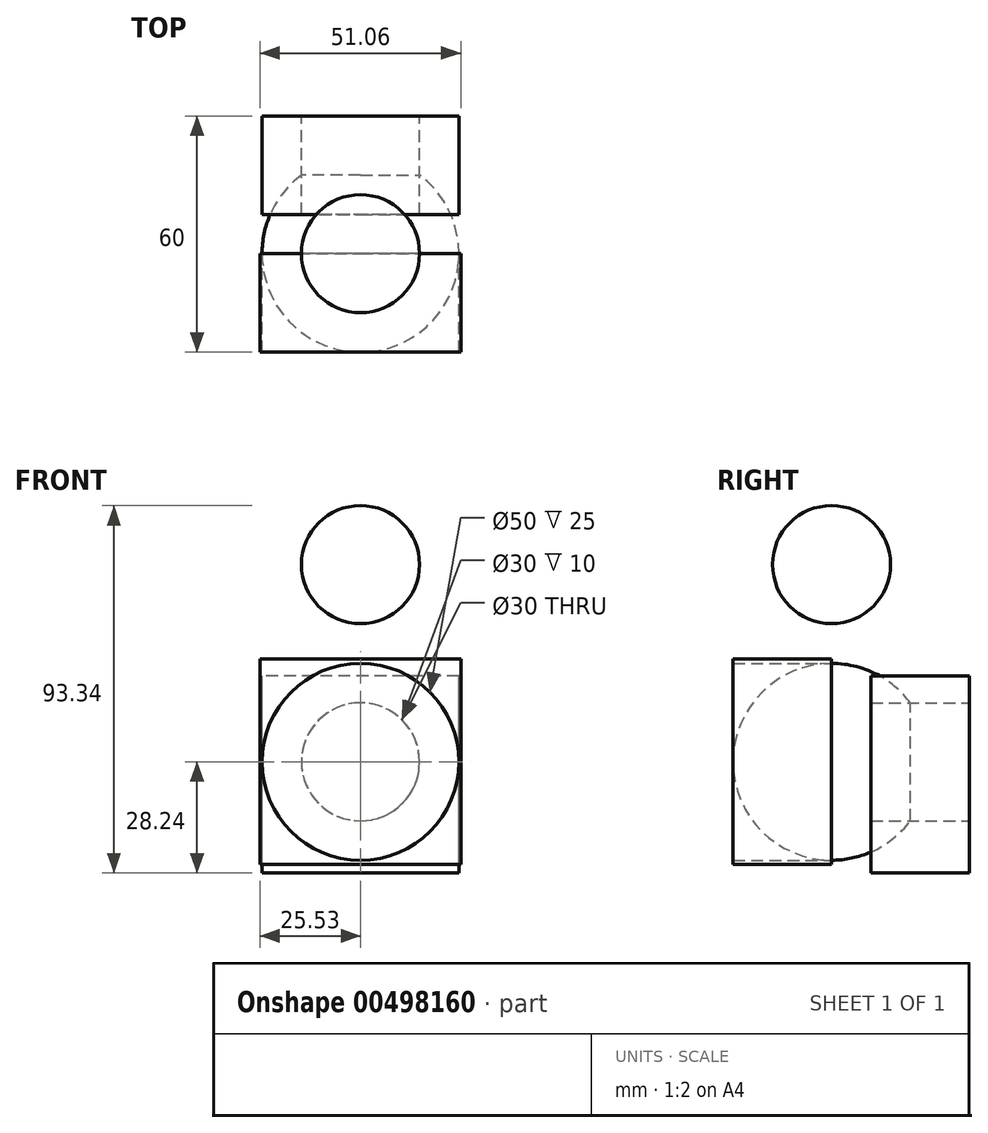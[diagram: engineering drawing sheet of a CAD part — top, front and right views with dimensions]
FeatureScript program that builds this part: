
annotation { "Feature Type Name" : "Feature", "Feature Type Description" : "" }
export const myFeature = defineFeature(function(context is Context, id is Id, definition is map)
    precondition{}
    {
        {
            var Q0;
            Q0=qCreatedBy(makeId("Front.planeOp"),FACE);
            var sketch = newSketch(context, id + "F0", { "sketchPlane" : qUnion([Q0])});
            skCircle(sketch, "E0", {"center": v(0, 0) * mm, "radius": 25 * mm});
            skLineSegment(sketch, "E1", {"start": v(0, 25) * mm, "end": v(0, -25) * mm});
            skLineSegment(sketch, "E2.bottom", {"start": v(25.53, 26.1) * mm, "end": v(-25.53, 26.1) * mm});
            skLineSegment(sketch, "E2.top", {"start": v(25.53, -26.1) * mm, "end": v(-25.53, -26.1) * mm});
            skLineSegment(sketch, "E2.left", {"start": v(25.53, 26.1) * mm, "end": v(25.53, -26.1) * mm});
            skLineSegment(sketch, "E2.right", {"start": v(-25.53, 26.1) * mm, "end": v(-25.53, -26.1) * mm});
            skSolve(sketch);
        }
        {
            var Q0;
            {var subQ0=sQuery(id+"F0.wireOp",EDGE,"E1");Q0=makeQuery(id+"F0.imprint","IMPRINT",FACE,{"disambiguationData":[TD([[makeQuery(id+"F0.imprint","IMPRINT",EDGE,{"derivedFrom":subQ0}),-1.0]])]});}
            var Q1;
            Q1=sQuery(id+"F0.wireOp",EDGE,"E1");
            revolve(context, id + "F1", {"entities" : qUnion([Q0]), "axis" : qUnion([Q1]), "revolveType" : RevolveType.FULL});
        }
        {
            var Q0;
            Q0 = qSketchRegion(id + "F0", true);
            extrude(context, id + "F2", {"entities" : qUnion([Q0]), "depth" : 25 * mm});
        }
        {
            var Q0;
            Q0=qCreatedBy(makeId("Front.planeOp"),FACE);
            var sketch = newSketch(context, id + "F3", { "sketchPlane" : qUnion([Q0])});
            skCircle(sketch, "E3", {"center": v(0, 50.1) * mm, "radius": 15 * mm});
            skLineSegment(sketch, "E4", {"start": v(0, 65.1) * mm, "end": v(0, 35.1) * mm});
            skSolve(sketch);
        }
        {
            var Q0;
            {var subQ0=sQuery(id+"F3.wireOp",EDGE,"E4");Q0=makeQuery(id+"F3.imprint","IMPRINT",FACE,{"disambiguationData":[TD([[makeQuery(id+"F3.imprint","IMPRINT",EDGE,{"derivedFrom":subQ0}),1.0]])]});}
            var Q1;
            Q1=sQuery(id+"F3.wireOp",EDGE,"E4");
            revolve(context, id + "F4", {"entities" : qUnion([Q0]), "axis" : qUnion([Q1]), "revolveType" : RevolveType.FULL});
        }
        {
            var Q0;
            Q0=makeQuery(id+"F2.opExtrude","CAP_FACE",FACE,{"disambiguationData":[OSD([sQuery(id+"F0.wireOp",EDGE,"E0"),sQuery(id+"F0.wireOp",EDGE,"E2.bottom"),sQuery(id+"F0.wireOp",EDGE,"E2.top"),sQuery(id+"F0.wireOp",EDGE,"E2.left"),sQuery(id+"F0.wireOp",EDGE,"E2.right")])],"isStart":true});
            cPlane(context, id + "F5", {"entities" : qUnion([Q0]), "cplaneType" : CPlaneType.OFFSET, "offset" : 10 * mm, "width" : 150 * mm, "height" : 150 * mm});
        }
        {
            var Q0;
            Q0=qCreatedBy(id+"F5.planeOp",FACE);
            var sketch = newSketch(context, id + "F6", { "sketchPlane" : qUnion([Q0])});
            skLineSegment(sketch, "E5.bottom", {"start": v(-25, -28.24) * mm, "end": v(25, -28.24) * mm});
            skLineSegment(sketch, "E5.top", {"start": v(-25, 21.76) * mm, "end": v(25, 21.76) * mm});
            skLineSegment(sketch, "E5.left", {"start": v(-25, -28.24) * mm, "end": v(-25, 21.76) * mm});
            skLineSegment(sketch, "E5.right", {"start": v(25, -28.24) * mm, "end": v(25, 21.76) * mm});
            skPoint(sketch, "E5.middle", {"position": v(0, -3.24) * mm});
            skSolve(sketch);
        }
        {
            var Q0;
            Q0=makeQuery(id+"F6.imprint","IMPRINT",FACE,{"disambiguationData":[TD([[makeQuery(id+"F6.imprint","IMPRINT",EDGE,{"derivedFrom":sQuery(id+"F6.wireOp",EDGE,"E5.bottom")}),1.0]])]});
            extrude(context, id + "F7", {"entities" : qUnion([Q0]), "depth" : 25 * mm});
        }
        {
            var Q0;
            Q0=makeQuery(id+"F7.opExtrude","CAP_FACE",FACE,{"disambiguationData":[OSD([sQuery(id+"F6.wireOp",EDGE,"E5.bottom"),sQuery(id+"F6.wireOp",EDGE,"E5.top"),sQuery(id+"F6.wireOp",EDGE,"E5.left"),sQuery(id+"F6.wireOp",EDGE,"E5.right")])],"isStart":false});
            var sketch = newSketch(context, id + "F8", { "sketchPlane" : qUnion([Q0])});
            skCircle(sketch, "E6", {"center": v(0, 0) * mm, "radius": 15 * mm});
            skSolve(sketch);
        }
        {
            var Q0;
            Q0=makeQuery(id+"F8.imprint","IMPRINT",FACE,{"disambiguationData":[TD([[makeQuery(id+"F8.imprint","IMPRINT",EDGE,{"derivedFrom":sQuery(id+"F8.wireOp",EDGE,"E6")}),1.0]])]});
            extrude(context, id + "F9", {"entities" : qUnion([Q0]), "operationType" : NewBodyOperationType.ADD, "depth" : 25 * mm});
        }
        {
            var Q0;
            Q0=makeQuery(id+"F9.opExtrude","CAP_FACE",FACE,{"disambiguationData":[OSD([sQuery(id+"F8.wireOp",EDGE,"E6")])],"isStart":false});
            extrude(context, id + "F10", {"entities" : qUnion([Q0]), "operationType" : NewBodyOperationType.REMOVE, "oppositeDirection" : true, "depth" : 50 * mm});
        }
    });
